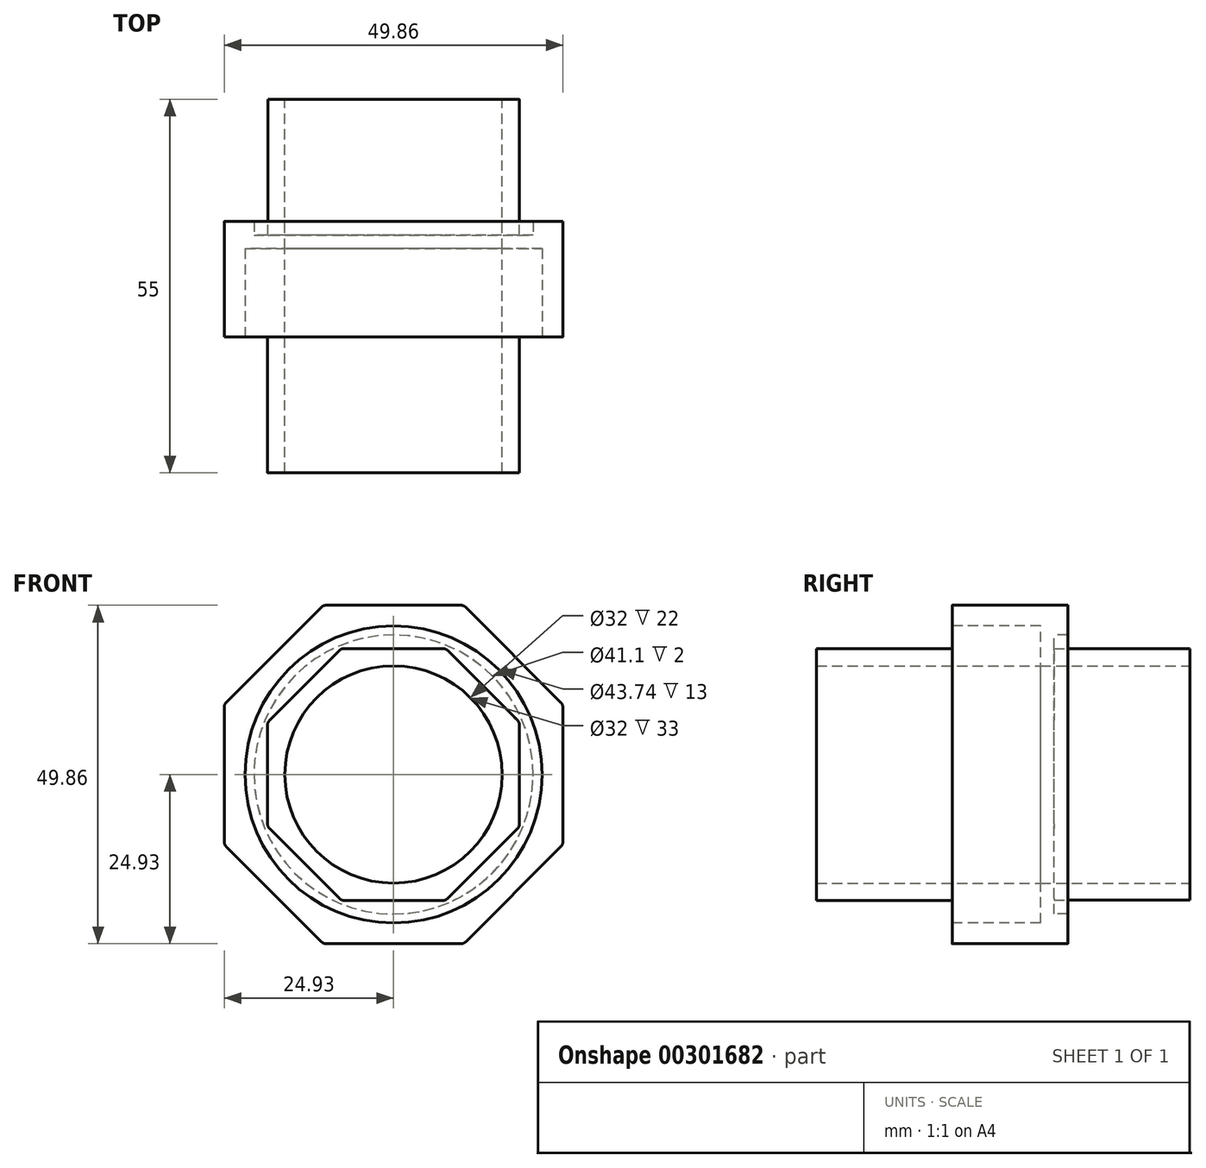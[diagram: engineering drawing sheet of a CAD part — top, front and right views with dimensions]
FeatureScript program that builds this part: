
annotation { "Feature Type Name" : "Feature", "Feature Type Description" : "" }
export const myFeature = defineFeature(function(context is Context, id is Id, definition is map)
    precondition{}
    {
        {
            var Q0;
            Q0=qCreatedBy(makeId("Front.planeOp"),FACE);
            var sketch = newSketch(context, id + "F0", { "sketchPlane" : qUnion([Q0])});
            skCircle(sketch, "E0", {"center": v(0, 0) * mm, "radius": 16 * mm});
            skCircle(sketch, "E1.cCircle", {"center": v(0, 0) * mm, "radius": 18.5 * mm, "construction": true});
            skLineSegment(sketch, "E1.0", {"start": v(-7.25, 18.5) * mm, "end": v(7.25, 18.5) * mm});
            skLineSegment(sketch, "E1.1", {"start": v(7.96, 18.2) * mm, "end": v(18.2, 7.96) * mm});
            skLineSegment(sketch, "E1.2", {"start": v(18.5, 7.25) * mm, "end": v(18.5, -7.25) * mm});
            skLineSegment(sketch, "E1.3", {"start": v(18.2, -7.96) * mm, "end": v(7.96, -18.2) * mm});
            skLineSegment(sketch, "E1.4", {"start": v(7.25, -18.5) * mm, "end": v(-7.25, -18.5) * mm});
            skLineSegment(sketch, "E1.5", {"start": v(-7.96, -18.2) * mm, "end": v(-18.2, -7.96) * mm});
            skLineSegment(sketch, "E1.6", {"start": v(-18.5, -7.25) * mm, "end": v(-18.5, 7.25) * mm});
            skLineSegment(sketch, "E1.7", {"start": v(-18.2, 7.96) * mm, "end": v(-7.96, 18.2) * mm});
            skPoint(sketch, "E1.0.midPoint", {"position": v(0, 18.5) * mm});
            skPoint(sketch, "E2.visualSharp", {"position": v(7.66, 18.5) * mm});
            skArc(sketch, "E2.filletArc", {"start": v(7.96, 18.2) * mm, "mid": v(7.63, 18.42) * mm, "end": v(7.25, 18.5) * mm});
            skPoint(sketch, "E3.visualSharp", {"position": v(-7.66, 18.5) * mm});
            skArc(sketch, "E3.filletArc", {"start": v(-7.25, 18.5) * mm, "mid": v(-7.63, 18.42) * mm, "end": v(-7.96, 18.2) * mm});
            skPoint(sketch, "E4.visualSharp", {"position": v(-18.5, 7.66) * mm});
            skArc(sketch, "E4.filletArc", {"start": v(-18.2, 7.96) * mm, "mid": v(-18.42, 7.63) * mm, "end": v(-18.5, 7.25) * mm});
            skPoint(sketch, "E5.visualSharp", {"position": v(-18.5, -7.66) * mm});
            skArc(sketch, "E5.filletArc", {"start": v(-18.5, -7.25) * mm, "mid": v(-18.42, -7.63) * mm, "end": v(-18.2, -7.96) * mm});
            skPoint(sketch, "E6.visualSharp", {"position": v(-7.66, -18.5) * mm});
            skArc(sketch, "E6.filletArc", {"start": v(-7.96, -18.2) * mm, "mid": v(-7.63, -18.42) * mm, "end": v(-7.25, -18.5) * mm});
            skPoint(sketch, "E7.visualSharp", {"position": v(7.66, -18.5) * mm});
            skArc(sketch, "E7.filletArc", {"start": v(7.25, -18.5) * mm, "mid": v(7.63, -18.42) * mm, "end": v(7.96, -18.2) * mm});
            skPoint(sketch, "E8.visualSharp", {"position": v(18.5, -7.66) * mm});
            skArc(sketch, "E8.filletArc", {"start": v(18.2, -7.96) * mm, "mid": v(18.42, -7.63) * mm, "end": v(18.5, -7.25) * mm});
            skPoint(sketch, "E9.visualSharp", {"position": v(18.5, 7.66) * mm});
            skArc(sketch, "E9.filletArc", {"start": v(18.5, 7.25) * mm, "mid": v(18.42, 7.63) * mm, "end": v(18.2, 7.96) * mm});
            skSolve(sketch);
        }
        {
            var Q0;
            Q0 = qSketchRegion(id + "F0", true);
            extrude(context, id + "F1", {"entities" : qUnion([Q0]), "depth" : 20 * mm});
        }
        {
            var Q0;
            Q0=makeQuery(id+"F1.opExtrude","CAP_FACE",FACE,{"disambiguationData":[OSD([sQuery(id+"F0.wireOp",EDGE,"TJ5j35M3-KHYs-10a6-pP0X-oIlg9sABvCHH"),sQuery(id+"F0.wireOp",EDGE,"E0")])],"isStart":false});
            var sketch = newSketch(context, id + "F2", { "sketchPlane" : qUnion([Q0])});
            skCircle(sketch, "E10", {"center": v(0, 0) * mm, "radius": 21.87 * mm});
            skCircle(sketch, "E11", {"center": v(0, 0) * mm, "radius": 16 * mm});
            skSolve(sketch);
        }
        {
            var Q0;
            Q0 = qSketchRegion(id + "F2", true);
            extrude(context, id + "F3", {"entities" : qUnion([Q0]), "operationType" : NewBodyOperationType.ADD, "depth" : 2 * mm});
        }
        {
            var Q0;
            Q0=makeQuery(id+"F3.opExtrude","CAP_FACE",FACE,{"disambiguationData":[OSD([sQuery(id+"F2.wireOp",EDGE,"E10"),sQuery(id+"F2.wireOp",EDGE,"E11")])],"isStart":true});
            var sketch = newSketch(context, id + "F4", { "sketchPlane" : qUnion([Q0])});
            skCircle(sketch, "E12", {"center": v(0, 0) * mm, "radius": 20.55 * mm});
            skCircle(sketch, "E13.cCircle", {"center": v(0, 0) * mm, "radius": 24.93 * mm, "construction": true});
            skLineSegment(sketch, "E13.0", {"start": v(-9.91, 24.93) * mm, "end": v(9.91, 24.93) * mm});
            skLineSegment(sketch, "E13.1", {"start": v(10.62, 24.63) * mm, "end": v(24.63, 10.62) * mm});
            skLineSegment(sketch, "E13.2", {"start": v(24.93, 9.91) * mm, "end": v(24.93, -9.91) * mm});
            skLineSegment(sketch, "E13.3", {"start": v(24.63, -10.62) * mm, "end": v(10.62, -24.63) * mm});
            skLineSegment(sketch, "E13.4", {"start": v(9.91, -24.93) * mm, "end": v(-9.91, -24.93) * mm});
            skLineSegment(sketch, "E13.5", {"start": v(-10.62, -24.63) * mm, "end": v(-24.63, -10.62) * mm});
            skLineSegment(sketch, "E13.6", {"start": v(-24.93, -9.91) * mm, "end": v(-24.93, 9.91) * mm});
            skLineSegment(sketch, "E13.7", {"start": v(-24.63, 10.62) * mm, "end": v(-10.62, 24.63) * mm});
            skPoint(sketch, "E13.0.midPoint", {"position": v(0, 24.93) * mm});
            skPoint(sketch, "E14.visualSharp", {"position": v(-10.33, 24.93) * mm});
            skArc(sketch, "E14.filletArc", {"start": v(-9.91, 24.93) * mm, "mid": v(-10.3, 24.85) * mm, "end": v(-10.62, 24.63) * mm});
            skPoint(sketch, "E15.visualSharp", {"position": v(10.33, 24.93) * mm});
            skArc(sketch, "E15.filletArc", {"start": v(10.62, 24.63) * mm, "mid": v(10.3, 24.85) * mm, "end": v(9.91, 24.93) * mm});
            skPoint(sketch, "E16.visualSharp", {"position": v(24.93, 10.33) * mm});
            skArc(sketch, "E16.filletArc", {"start": v(24.93, 9.91) * mm, "mid": v(24.85, 10.3) * mm, "end": v(24.63, 10.62) * mm});
            skPoint(sketch, "E17.visualSharp", {"position": v(-24.93, 10.33) * mm});
            skArc(sketch, "E17.filletArc", {"start": v(-24.63, 10.62) * mm, "mid": v(-24.85, 10.3) * mm, "end": v(-24.93, 9.91) * mm});
            skPoint(sketch, "E18.visualSharp", {"position": v(-24.93, -10.33) * mm});
            skArc(sketch, "E18.filletArc", {"start": v(-24.93, -9.91) * mm, "mid": v(-24.85, -10.3) * mm, "end": v(-24.63, -10.62) * mm});
            skPoint(sketch, "E19.visualSharp", {"position": v(-10.33, -24.93) * mm});
            skArc(sketch, "E19.filletArc", {"start": v(-10.62, -24.63) * mm, "mid": v(-10.3, -24.85) * mm, "end": v(-9.91, -24.93) * mm});
            skPoint(sketch, "E20.visualSharp", {"position": v(10.33, -24.93) * mm});
            skArc(sketch, "E20.filletArc", {"start": v(9.91, -24.93) * mm, "mid": v(10.3, -24.85) * mm, "end": v(10.62, -24.63) * mm});
            skPoint(sketch, "E21.visualSharp", {"position": v(24.93, -10.33) * mm});
            skArc(sketch, "E21.filletArc", {"start": v(24.63, -10.62) * mm, "mid": v(24.85, -10.3) * mm, "end": v(24.93, -9.91) * mm});
            skSolve(sketch);
        }
        {
            var Q0;
            Q0=makeQuery(id+"F4.imprint","IMPRINT",FACE,{"disambiguationData":[TD([[makeQuery(id+"F4.imprint","IMPRINT",EDGE,{"derivedFrom":sQuery(id+"F4.wireOp",EDGE,"E13.0")}),-1.0]])]});
            var Q1;
            Q1=makeQuery(id+"F4.imprint","IMPRINT",FACE,{"disambiguationData":[TD([[makeQuery(id+"F4.imprint","IMPRINT",EDGE,{"derivedFrom":sQuery(id+"F4.wireOp",EDGE,"E12")}),-1.0]])]});
            extrude(context, id + "F5", {"entities" : qUnion([Q0, Q1]), "depth" : 2 * mm});
        }
        {
            var Q0;
            Q0=makeQuery(id+"F5.opExtrude","CAP_FACE",FACE,{"disambiguationData":[OSD([sQuery(id+"F4.wireOp",EDGE,"E12"),sQuery(id+"F4.wireOp",EDGE,"E13.0"),sQuery(id+"F4.wireOp",EDGE,"E13.1"),sQuery(id+"F4.wireOp",EDGE,"E13.2"),sQuery(id+"F4.wireOp",EDGE,"E13.3"),sQuery(id+"F4.wireOp",EDGE,"E13.4"),sQuery(id+"F4.wireOp",EDGE,"E13.5"),sQuery(id+"F4.wireOp",EDGE,"E13.6"),sQuery(id+"F4.wireOp",EDGE,"E13.7"),sQuery(id+"F4.wireOp",EDGE,"E14.filletArc"),sQuery(id+"F4.wireOp",EDGE,"E15.filletArc"),sQuery(id+"F4.wireOp",EDGE,"E16.filletArc"),sQuery(id+"F4.wireOp",EDGE,"E17.filletArc"),sQuery(id+"F4.wireOp",EDGE,"E18.filletArc"),sQuery(id+"F4.wireOp",EDGE,"E19.filletArc"),sQuery(id+"F4.wireOp",EDGE,"E20.filletArc"),sQuery(id+"F4.wireOp",EDGE,"E21.filletArc")])],"isStart":true});
            extrude(context, id + "F6", {"entities" : qUnion([Q0]), "operationType" : NewBodyOperationType.ADD, "depth" : 15 * mm});
        }
        {
            var Q0;
            Q0=makeQuery(id+"F6.opExtrude","CAP_FACE",FACE,{"disambiguationData":[OSD([sQuery(id+"F4.wireOp",EDGE,"E12"),sQuery(id+"F4.wireOp",EDGE,"E13.0"),sQuery(id+"F4.wireOp",EDGE,"E13.1"),sQuery(id+"F4.wireOp",EDGE,"E13.2"),sQuery(id+"F4.wireOp",EDGE,"E13.3"),sQuery(id+"F4.wireOp",EDGE,"E13.4"),sQuery(id+"F4.wireOp",EDGE,"E13.5"),sQuery(id+"F4.wireOp",EDGE,"E13.6"),sQuery(id+"F4.wireOp",EDGE,"E13.7"),sQuery(id+"F4.wireOp",EDGE,"E14.filletArc"),sQuery(id+"F4.wireOp",EDGE,"E15.filletArc"),sQuery(id+"F4.wireOp",EDGE,"E16.filletArc"),sQuery(id+"F4.wireOp",EDGE,"E17.filletArc"),sQuery(id+"F4.wireOp",EDGE,"E18.filletArc"),sQuery(id+"F4.wireOp",EDGE,"E19.filletArc"),sQuery(id+"F4.wireOp",EDGE,"E20.filletArc"),sQuery(id+"F4.wireOp",EDGE,"E21.filletArc")])],"isStart":false});
            var sketch = newSketch(context, id + "F7", { "sketchPlane" : qUnion([Q0])});
            skCircle(sketch, "E22", {"center": v(0, 0) * mm, "radius": 21.87 * mm});
            skSolve(sketch);
        }
        {
            var Q0;
            Q0 = qSketchRegion(id + "F7", true);
            extrude(context, id + "F8", {"entities" : qUnion([Q0]), "operationType" : NewBodyOperationType.REMOVE, "oppositeDirection" : true, "depth" : 13 * mm});
        }
        {
            var Q0;
            Q0=makeQuery(id+"F3.opExtrude","CAP_FACE",FACE,{"disambiguationData":[OSD([sQuery(id+"F2.wireOp",EDGE,"E10"),sQuery(id+"F2.wireOp",EDGE,"E11")])],"isStart":false});
            var sketch = newSketch(context, id + "F9", { "sketchPlane" : qUnion([Q0])});
            skCircle(sketch, "E23", {"center": v(0, 0) * mm, "radius": 21.87 * mm});
            skCircle(sketch, "E24", {"center": v(0, 0) * mm, "radius": 16 * mm});
            skSolve(sketch);
        }
        {
            var Q0;
            Q0 = qSketchRegion(id + "F9", true);
            extrude(context, id + "F10", {"entities" : qUnion([Q0]), "depth" : 13 * mm});
        }
        {
            var Q0;
            Q0=makeQuery(id+"F10.opExtrude","CAP_FACE",FACE,{"disambiguationData":[OSD([sQuery(id+"F9.wireOp",EDGE,"E23"),sQuery(id+"F9.wireOp",EDGE,"E24")])],"isStart":false});
            var sketch = newSketch(context, id + "F11", { "sketchPlane" : qUnion([Q0])});
            skCircle(sketch, "E25.cCircle", {"center": v(0, 0) * mm, "radius": 18.55 * mm, "construction": true});
            skLineSegment(sketch, "E25.0", {"start": v(-7.27, 18.55) * mm, "end": v(7.27, 18.55) * mm});
            skLineSegment(sketch, "E25.1", {"start": v(7.98, 18.26) * mm, "end": v(18.26, 7.98) * mm});
            skLineSegment(sketch, "E25.2", {"start": v(18.55, 7.27) * mm, "end": v(18.55, -7.23) * mm});
            skLineSegment(sketch, "E25.3", {"start": v(18.23, -8) * mm, "end": v(7.98, -18.26) * mm});
            skLineSegment(sketch, "E25.4", {"start": v(7.27, -18.55) * mm, "end": v(-7.27, -18.55) * mm});
            skLineSegment(sketch, "E25.5", {"start": v(-7.98, -18.26) * mm, "end": v(-18.26, -7.98) * mm});
            skLineSegment(sketch, "E25.6", {"start": v(-18.55, -7.27) * mm, "end": v(-18.55, 7.27) * mm});
            skLineSegment(sketch, "E25.7", {"start": v(-18.26, 7.98) * mm, "end": v(-7.98, 18.26) * mm});
            skPoint(sketch, "E25.0.midPoint", {"position": v(0, 18.55) * mm});
            skCircle(sketch, "E26", {"center": v(0, 0) * mm, "radius": 16 * mm});
            skPoint(sketch, "E27.visualSharp", {"position": v(-7.68, 18.55) * mm});
            skArc(sketch, "E27.filletArc", {"start": v(-7.27, 18.55) * mm, "mid": v(-7.65, 18.47) * mm, "end": v(-7.98, 18.26) * mm});
            skPoint(sketch, "E28.visualSharp", {"position": v(7.68, 18.55) * mm});
            skArc(sketch, "E28.filletArc", {"start": v(7.98, 18.26) * mm, "mid": v(7.65, 18.47) * mm, "end": v(7.27, 18.55) * mm});
            skPoint(sketch, "E29.visualSharp", {"position": v(18.55, 7.68) * mm});
            skArc(sketch, "E29.filletArc", {"start": v(18.55, 7.27) * mm, "mid": v(18.47, 7.65) * mm, "end": v(18.26, 7.98) * mm});
            skPoint(sketch, "E30.visualSharp", {"position": v(18.55, -7.68) * mm});
            skArc(sketch, "E30.filletArc", {"start": v(18.23, -8) * mm, "mid": v(18.47, -7.65) * mm, "end": v(18.55, -7.23) * mm});
            skPoint(sketch, "E31.visualSharp", {"position": v(7.68, -18.55) * mm});
            skArc(sketch, "E31.filletArc", {"start": v(7.27, -18.55) * mm, "mid": v(7.65, -18.47) * mm, "end": v(7.98, -18.26) * mm});
            skPoint(sketch, "E32.visualSharp", {"position": v(-7.68, -18.55) * mm});
            skArc(sketch, "E32.filletArc", {"start": v(-7.98, -18.26) * mm, "mid": v(-7.65, -18.47) * mm, "end": v(-7.27, -18.55) * mm});
            skPoint(sketch, "E33.visualSharp", {"position": v(-18.55, -7.68) * mm});
            skArc(sketch, "E33.filletArc", {"start": v(-18.55, -7.27) * mm, "mid": v(-18.47, -7.65) * mm, "end": v(-18.26, -7.98) * mm});
            skPoint(sketch, "E34.visualSharp", {"position": v(-18.55, 7.68) * mm});
            skArc(sketch, "E34.filletArc", {"start": v(-18.26, 7.98) * mm, "mid": v(-18.47, 7.65) * mm, "end": v(-18.55, 7.27) * mm});
            skSolve(sketch);
        }
        {
            var Q0;
            Q0 = qSketchRegion(id + "F11", true);
            extrude(context, id + "F12", {"entities" : qUnion([Q0]), "operationType" : NewBodyOperationType.ADD, "depth" : 20 * mm});
        }
    });
